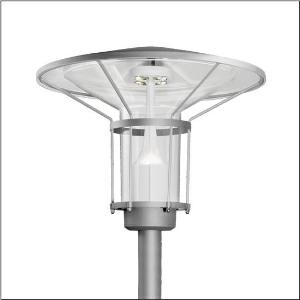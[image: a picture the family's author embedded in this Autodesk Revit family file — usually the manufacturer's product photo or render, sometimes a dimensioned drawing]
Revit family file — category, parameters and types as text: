
# Revit family: laterne_classic___st1_2a_5xa5243ab14h_e952
name_source: partatom
category: Lighting Fixtures
units: mm (PartAtom-declared; Revit-internal decimal feet)

## family parameters
Cut with Voids When Loaded = No
Host = Face
Light Source = No
Part Type = Normal
Room Calculation Point = No
Round Connector Dimension = Use Diameter
Shared = No

## types (1)
- --- (1 x LED, 1380 lm, 14.9 W, 2200K)
    Apparent Load = 15 VA
    CIE Flux Codes = 21 60 93 97 100
    Color Rendering = 70
    Color Temperature = 2200K
    Default Elevation = 1800 mm
    Description = Lantern Classic, mast luminaire, Module 540 Plus, primary light control with 3 zone facetted reflector, of plastic, silver coated, highly specular, structured, primary optical cover: cover, of PMMA, transparent, light distribution: ST1.2a, light emission: direct distribution, primary light characteristic: asymmetric, installation type: post-top, LED, High Power LED, rated luminous flux: 1.380lm, luminous efficacy: 93lm/W, light colour: 722, colour temperature: 2200K, control gear: ECG Plus, control: flexible luminous flux parameterisation, time-dependent luminous flux control, digital communication interface, power reduction, overheat protection, constant luminous flux control, electronic power reduction, with terminal, 6-pole, max. 2.5mm², mains connection: 230..240V, AC, 50/60Hz, start of lifetime: 15W, end of service life: 16W, reduction: 7W, luminaire housing, upper part, of glass-fibre reinforced polyester, coated, Siteco® metallic grey (DB 702S), diameter: 750mm, height: 596mm, spigot size: d x l = 76 x 70mm (post-top) | with reducer (optional accessory) 60 x 70mm, post-top mast mounting element, of diecast aluminium, coated, Siteco® metallic grey (DB 702S), Module 540 Plus, traffic white (RAL 9016), equipment: standard, protection rating (complete): IP65, insulation class (complete): insulation class II (safety insulation), certification: CE, ENEC, VDE, packaging unit: 1 piece

Light Distribution: ST1.2a
    Height = 596 mm
    Lamp = 1 x LED
    Lamp Light Flux = 1380 lm
    Lamp Power = 14.9 W
    Lamp count = 1
    Length = 750 mm
    Luminous efficacy = 93 lm/W
    Manufacturer = Siteco
    ModVariant = No
    Model = 5XA5243AB14H
    Number of Poles = 1
    OnlyDefault = Yes
    Power Factor = 1
    Product Name = Laterne Classic | ST1.2a
    Product group = mast luminaire | pylon top
    ProductGroupID = 6100
    Protection Class = Protection class II
    Protection Degree = IP 65
    RLX_Detail_Level = 1
    RLX_Emergency_Light_Flux = 0 lm
    RLX_Emergency_Type = 0
    RLX_Emergency_Type_DB = No
    RlxData = <blob elided: 92685 chars, md5=b9e2b276>
    Socket = socket
    Standby Power = 0 W
    System Light Flux = 1380 lm
    System Power = 15 W
    Type Comments = factory setting: luminous flux: 100 % | dim-lin: 254 | 570 mA
    Type Image = l_1006052.jpg
    URL = http://relux.com
    VarID = @adj_173576
    Voltage = 0 V
    Weight = 0.00 kg
    Width = 0 mm  [stored 0 ft]

note: [stored X ft] marks values corroborated as IEEE doubles in the binary element streams (Revit-internal decimal feet)

## geometry (parser evidence)
native form markers: Blend x4, Sweep x11
no freeform markers — native parametric forms only
